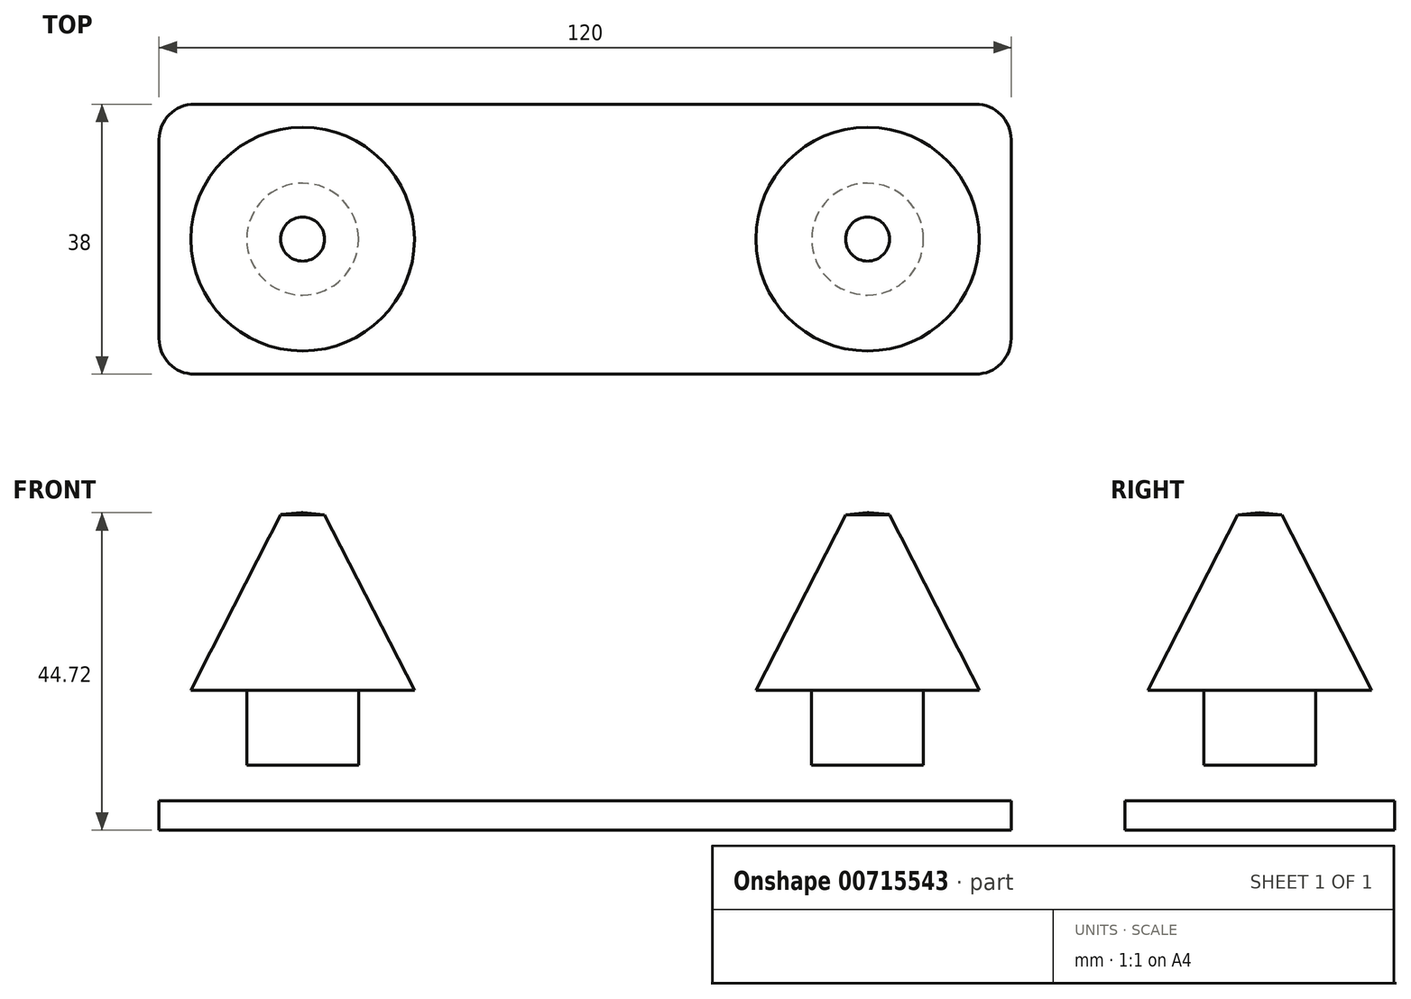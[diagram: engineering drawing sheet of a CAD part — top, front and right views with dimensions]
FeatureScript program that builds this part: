
annotation { "Feature Type Name" : "Feature", "Feature Type Description" : "" }
export const myFeature = defineFeature(function(context is Context, id is Id, definition is map)
    precondition{}
    {
        {
            var Q0;
            Q0=qCreatedBy(makeId("Front.planeOp"),FACE);
            var sketch = newSketch(context, id + "F0", { "sketchPlane" : qUnion([Q0])});
            skLineSegment(sketch, "E0", {"start": v(0, 34.71) * mm, "end": v(0, 0) * mm, "construction": true});
            skLineSegment(sketch, "E1", {"start": v(0, 0) * mm, "end": v(-73.5, 0) * mm, "construction": true});
            skLineSegment(sketch, "E2.bottom", {"start": v(-47.64, 0) * mm, "end": v(-39.77, 0) * mm});
            skLineSegment(sketch, "E2.top", {"start": v(-65.07, -11.95) * mm, "end": v(66.2, -11.95) * mm});
            skLineSegment(sketch, "E2.left", {"start": v(-65.07, 0) * mm, "end": v(-65.07, -11.95) * mm});
            skLineSegment(sketch, "E2.right", {"start": v(66.2, 0) * mm, "end": v(66.2, -11.95) * mm});
            skLineSegment(sketch, "E3", {"start": v(-39.77, 35.56) * mm, "end": v(-39.77, 0) * mm, "construction": true});
            skLineSegment(sketch, "E4", {"start": v(-39.77, 0) * mm, "end": v(-47.64, 0) * mm});
            skLineSegment(sketch, "E5", {"start": v(-47.64, 0) * mm, "end": v(-47.64, 10.54) * mm});
            skLineSegment(sketch, "E6", {"start": v(-47.64, 10.54) * mm, "end": v(-55.51, 10.54) * mm});
            skLineSegment(sketch, "E7", {"start": v(-55.51, 10.54) * mm, "end": v(-42.86, 35.27) * mm});
            skLineSegment(sketch, "E8", {"start": v(-42.86, 35.27) * mm, "end": v(-39.77, 35.56) * mm});
            skLineSegment(sketch, "E9", {"start": v(-39.77, 35.56) * mm, "end": v(-39.77, 0) * mm});
            skLineSegment(sketch, "E10.trimOffspring", {"start": v(0, 0) * mm, "end": v(66.2, 0) * mm});
            skLineSegment(sketch, "E11", {"start": v(-39.77, -38.65) * mm, "end": v(-39.77, 66.76) * mm, "construction": true});
            skSolve(sketch);
        }
        {
            var Q0;
            Q0=makeQuery(id+"F0.imprint","IMPRINT",FACE,{"disambiguationData":[TD([[makeQuery(id+"F0.imprint","IMPRINT",EDGE,{"derivedFrom":sQuery(id+"F0.wireOp",EDGE,"E5")}),-1.0]])]});
            var Q1;
            Q1=sQuery(id+"F0.wireOp",EDGE,"E11");
            revolve(context, id + "F1", {"surfaceOperationType" : NewSurfaceOperationType.NEW, "entities" : qUnion([Q0]), "axis" : qUnion([Q1]), "revolveType" : RevolveType.FULL});
        }
        {
            var Q0;
            Q0=makeQuery(id+"F1.opRevolve","SWEPT_BODY",BODY,{"disambiguationData":[OSD([sQuery(id+"F0.wireOp",EDGE,"E5"),sQuery(id+"F0.wireOp",EDGE,"E6"),sQuery(id+"F0.wireOp",EDGE,"E7"),sQuery(id+"F0.wireOp",EDGE,"E8"),sQuery(id+"F0.wireOp",EDGE,"E4"),sQuery(id+"F0.wireOp",EDGE,"E9")])]});
            var Q1;
            Q1=qCreatedBy(makeId("Right.planeOp"),FACE);
            mirror(context, id + "F2", {"operationType" : NewBodyOperationType.ADD, "entities" : qUnion([Q0]), "mirrorPlane" : qUnion([Q1])});
        }
        {
            var Q0;
            Q0=qCreatedBy(makeId("Top.planeOp"),FACE);
            var sketch = newSketch(context, id + "F3", { "sketchPlane" : qUnion([Q0])});
            skLineSegment(sketch, "E12", {"start": v(49.72, 0) * mm, "end": v(-49.91, 0) * mm, "construction": true});
            skLineSegment(sketch, "E13", {"start": v(-60, 0) * mm, "end": v(-60, 19) * mm});
            skLineSegment(sketch, "E14", {"start": v(-60, 19) * mm, "end": v(60, 19) * mm});
            skLineSegment(sketch, "E15", {"start": v(60, 19) * mm, "end": v(60, -19) * mm});
            skLineSegment(sketch, "E16", {"start": v(60, -19) * mm, "end": v(-60, -19) * mm});
            skLineSegment(sketch, "E17", {"start": v(-60, -19) * mm, "end": v(-60, 0) * mm});
            skSolve(sketch);
        }
        {
            var Q0;
            Q0 = qSketchRegion(id + "F3", true);
            extrude(context, id + "F4", {"entities" : qUnion([Q0]), "oppositeDirection" : true, "depth" : 21 * mm, "offsetDistance" : 25 * mm});
        }
        {
            var Q0;
            Q0=makeQuery(id+"F4.opExtrude","SWEPT_EDGE",EDGE,{"disambiguationData":[OSD([sQuery(id+"F3.wireOp",EDGE,"E15"),sQuery(id+"F3.wireOp",EDGE,"E16")])]});
            var Q1;
            Q1=makeQuery(id+"F4.opExtrude","SWEPT_EDGE",EDGE,{"disambiguationData":[OSD([sQuery(id+"F3.wireOp",EDGE,"E16"),sQuery(id+"F3.wireOp",EDGE,"E17")])]});
            var Q2;
            Q2=makeQuery(id+"F4.opExtrude","SWEPT_EDGE",EDGE,{"disambiguationData":[OSD([sQuery(id+"F3.wireOp",EDGE,"E14"),sQuery(id+"F3.wireOp",EDGE,"E15")])]});
            var Q3;
            Q3=makeQuery(id+"F4.opExtrude","SWEPT_EDGE",EDGE,{"disambiguationData":[OSD([sQuery(id+"F3.wireOp",EDGE,"E13"),sQuery(id+"F3.wireOp",EDGE,"E14")])]});
            fillet(context, id + "F5", {"entities" : qUnion([Q0, Q1, Q2, Q3]), "radius" : 5 * mm, "tangentPropagation" : true, "allowEdgeOverflow" : false});
        }
        {
            var Q0;
            Q0 = qSketchRegion(id + "F3", true);
            extrude(context, id + "F6", {"entities" : qUnion([Q0]), "operationType" : NewBodyOperationType.REMOVE, "oppositeDirection" : true, "depth" : 5 * mm, "offsetDistance" : 25 * mm});
        }
        {
            var Q0;
            Q0=qCreatedBy(makeId("Front.planeOp"),FACE);
            var sketch = newSketch(context, id + "F7", { "sketchPlane" : qUnion([Q0])});
            skLineSegment(sketch, "E18.bottom", {"start": v(-85.01, -9.16) * mm, "end": v(80.3, -9.16) * mm});
            skLineSegment(sketch, "E18.top", {"start": v(-85.01, -28.76) * mm, "end": v(80.3, -28.76) * mm});
            skLineSegment(sketch, "E18.left", {"start": v(-85.01, -9.16) * mm, "end": v(-85.01, -28.76) * mm});
            skLineSegment(sketch, "E18.right", {"start": v(80.3, -9.16) * mm, "end": v(80.3, -28.76) * mm});
            skSolve(sketch);
        }
        {
            var Q0;
            Q0=makeQuery(id+"F7.imprint","IMPRINT",FACE,{"disambiguationData":[TD([[makeQuery(id+"F7.imprint","IMPRINT",EDGE,{"derivedFrom":sQuery(id+"F7.wireOp",EDGE,"E18.bottom")}),-1.0]])]});
            extrude(context, id + "F8", {"entities" : qUnion([Q0]), "operationType" : NewBodyOperationType.REMOVE, "endBound" : BoundingType.THROUGH_ALL, "oppositeDirection" : true, "depth" : 25 * mm, "offsetDistance" : 25 * mm});
        }
        {
            var Q0;
            Q0=makeQuery(id+"F8.boolean.opBoolean","COPY",FACE,{"derivedFrom":makeQuery(id+"F8.opExtrude","CAP_FACE",FACE,{"disambiguationData":[OSD([sQuery(id+"F7.wireOp",EDGE,"E18.bottom"),sQuery(id+"F7.wireOp",EDGE,"E18.top"),sQuery(id+"F7.wireOp",EDGE,"E18.left"),sQuery(id+"F7.wireOp",EDGE,"E18.right")])],"isStart":true})});
            extrude(context, id + "F9", {"entities" : qUnion([Q0]), "operationType" : NewBodyOperationType.REMOVE, "endBound" : BoundingType.THROUGH_ALL, "oppositeDirection" : true, "depth" : 25 * mm, "offsetDistance" : 25 * mm});
        }
    });
